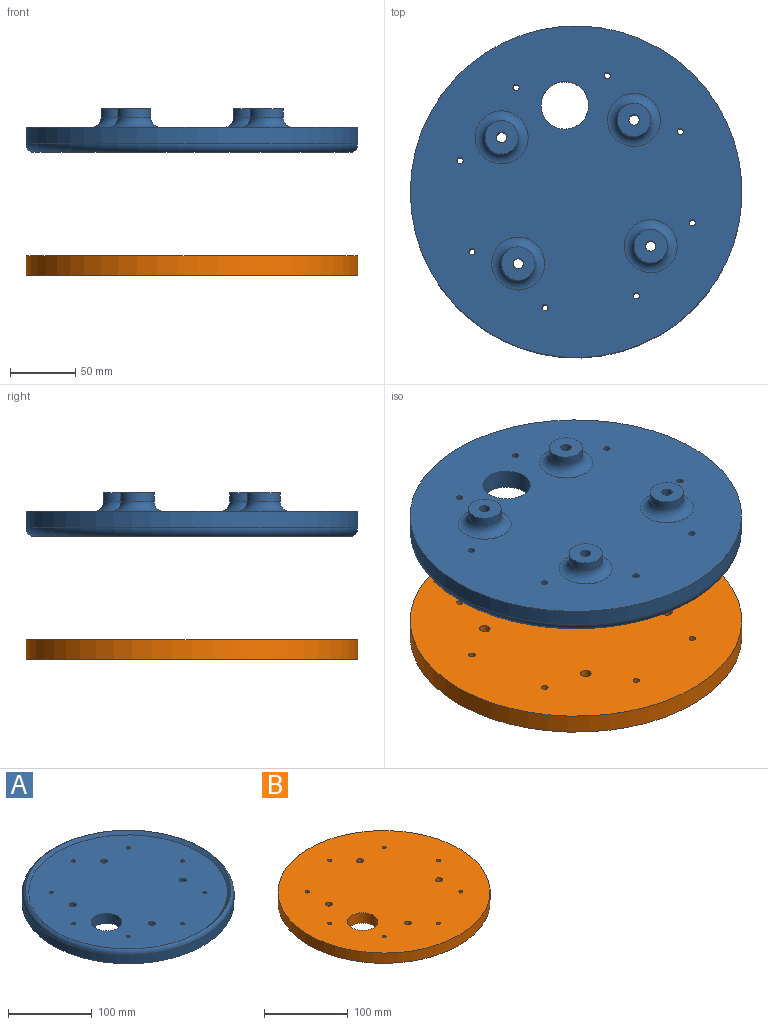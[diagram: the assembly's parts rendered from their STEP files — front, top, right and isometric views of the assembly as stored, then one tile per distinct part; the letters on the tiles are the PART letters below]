
ASSEMBLY  parts=2 mates=1
PART A: 30 faces, bbox 274.9x274.9x34.1 mm
  f0: plane 238.13x238.13mm, normal (0,0,1), area 43147.3mm2, adj f3,f4,f5,f6,f7,f8,f9,f10
  f1: cylinder r=127mm len=254mm, axis (0,0,-1), area 10034.5mm2, adj f2,f27
  f2: plane 254x254mm, normal (0,0,-1), area 44292.5mm2, adj f1,f3,f4,f5,f6,f7,f8,f9
  f3: cylinder r=2.38mm len=15mm, axis (0,0,1), area 224.4mm2, adj f0,f2
  f4: cylinder r=2.38mm len=15mm, axis (0,0,1), area 224.4mm2, adj f0,f2
  f5: cylinder r=2.38mm len=15mm, axis (0,0,1), area 224.4mm2, adj f0,f2
  f6: cylinder r=2.38mm len=15mm, axis (0,0,1), area 224.4mm2, adj f0,f2
  f7: cylinder r=2.38mm len=15mm, axis (0,0,1), area 224.4mm2, adj f0,f2
  f8: cylinder r=2.38mm len=15mm, axis (0,0,1), area 224.4mm2, adj f0,f2
  f9: cylinder r=2.38mm len=15mm, axis (0,0,1), area 224.4mm2, adj f0,f2
  f10: cylinder r=2.38mm len=15mm, axis (0,0,1), area 224.4mm2, adj f0,f2
  f11: cylinder r=3.97mm len=29.29mm, axis (0,0,1), area 730.3mm2, adj f0,f25
  f12: cylinder r=3.97mm len=29.29mm, axis (0,0,1), area 730.3mm2, adj f0,f22
  f13: cylinder r=3.97mm len=29.29mm, axis (0,0,1), area 730.3mm2, adj f0,f19
  f14: cylinder r=3.97mm len=29.29mm, axis (0,0,1), area 730.3mm2, adj f0,f16
  f15: cylinder r=12.7mm len=25.4mm, axis (0,0,1), area 532mm2, adj f16,f17
  f16: plane 25.4x25.4mm, normal (0,0,-1), area 457.2mm2, adj f14,f15
  f17: torus R=20.32mm, axis (0,0,1), area 1163.4mm2, adj f2,f15
  f18: cylinder r=12.7mm len=25.4mm, axis (0,0,1), area 532mm2, adj f19,f20
  f19: plane 25.4x25.4mm, normal (0,0,-1), area 457.2mm2, adj f13,f18
  f20: torus R=20.32mm, axis (0,0,1), area 1163.4mm2, adj f2,f18
  f21: torus R=20.32mm, axis (0,0,1), area 1163.4mm2, adj f2,f23
  f22: plane 25.4x25.4mm, normal (0,0,-1), area 457.2mm2, adj f12,f23
  f23: cylinder r=12.7mm len=25.4mm, axis (0,0,1), area 532mm2, adj f21,f22
  f24: cylinder r=12.7mm len=25.4mm, axis (0,0,1), area 532mm2, adj f25,f26
  f25: plane 25.4x25.4mm, normal (0,0,-1), area 457.2mm2, adj f11,f24
  f26: torus R=20.32mm, axis (0,0,1), area 1163.4mm2, adj f2,f24
  f27: torus R=119.76mm, axis (0,0,1), area 6260mm2, adj f1,f28
  f28: cone r=114.3mm half-angle=45deg, axis (0,0,1), area 4317.1mm2, adj f0,f27
  f29: cylinder r=18.26mm len=36.51mm, axis (0,0,1), area 1720.6mm2, adj f0,f2
PART B: 16 faces, bbox 254x254x15 mm
  f0: cylinder r=127mm len=254mm, axis (0,0,-1), area 11969.5mm2, adj f1,f2
  f1: plane 254x254mm, normal (0,0,1), area 49283.2mm2, adj f0,f3,f4,f5,f6,f7,f8,f9
  f2: plane 254x254mm, normal (0,0,-1), area 49283.2mm2, adj f0,f3,f4,f5,f6,f7,f8,f9
  f3: cylinder r=2.38mm len=15mm, axis (0,0,1), area 224.4mm2, adj f1,f2
  f4: cylinder r=2.38mm len=15mm, axis (0,0,1), area 224.4mm2, adj f1,f2
  f5: cylinder r=2.38mm len=15mm, axis (0,0,1), area 224.4mm2, adj f1,f2
  f6: cylinder r=2.38mm len=15mm, axis (0,0,1), area 224.4mm2, adj f1,f2
  f7: cylinder r=2.38mm len=15mm, axis (0,0,1), area 224.4mm2, adj f1,f2
  f8: cylinder r=2.38mm len=15mm, axis (0,0,1), area 224.4mm2, adj f1,f2
  f9: cylinder r=2.38mm len=15mm, axis (0,0,1), area 224.4mm2, adj f1,f2
  f10: cylinder r=2.38mm len=15mm, axis (0,0,1), area 224.4mm2, adj f1,f2
  f11: cylinder r=3.97mm len=15mm, axis (0,0,1), area 374mm2, adj f1,f2
  f12: cylinder r=3.97mm len=15mm, axis (0,0,1), area 374mm2, adj f1,f2
  f13: cylinder r=3.97mm len=15mm, axis (0,0,1), area 374mm2, adj f1,f2
  f14: cylinder r=3.97mm len=15mm, axis (0,0,1), area 374mm2, adj f1,f2
  f15: cylinder r=18.26mm len=36.51mm, axis (0,0,1), area 1720.6mm2, adj f1,f2
PLACE A rot(axis=(0.87,-0.5,0),180deg) t=(-204.81,101.83,230.36)mm fixed
PLACE B rot(axis=(0.87,-0.5,0),180deg) t=(-204.78,101.63,132.15)mm
MATE slider B.f2 <-> A.f0  axis (0,0,1) through (-204.6,100.22,132.15)mm
